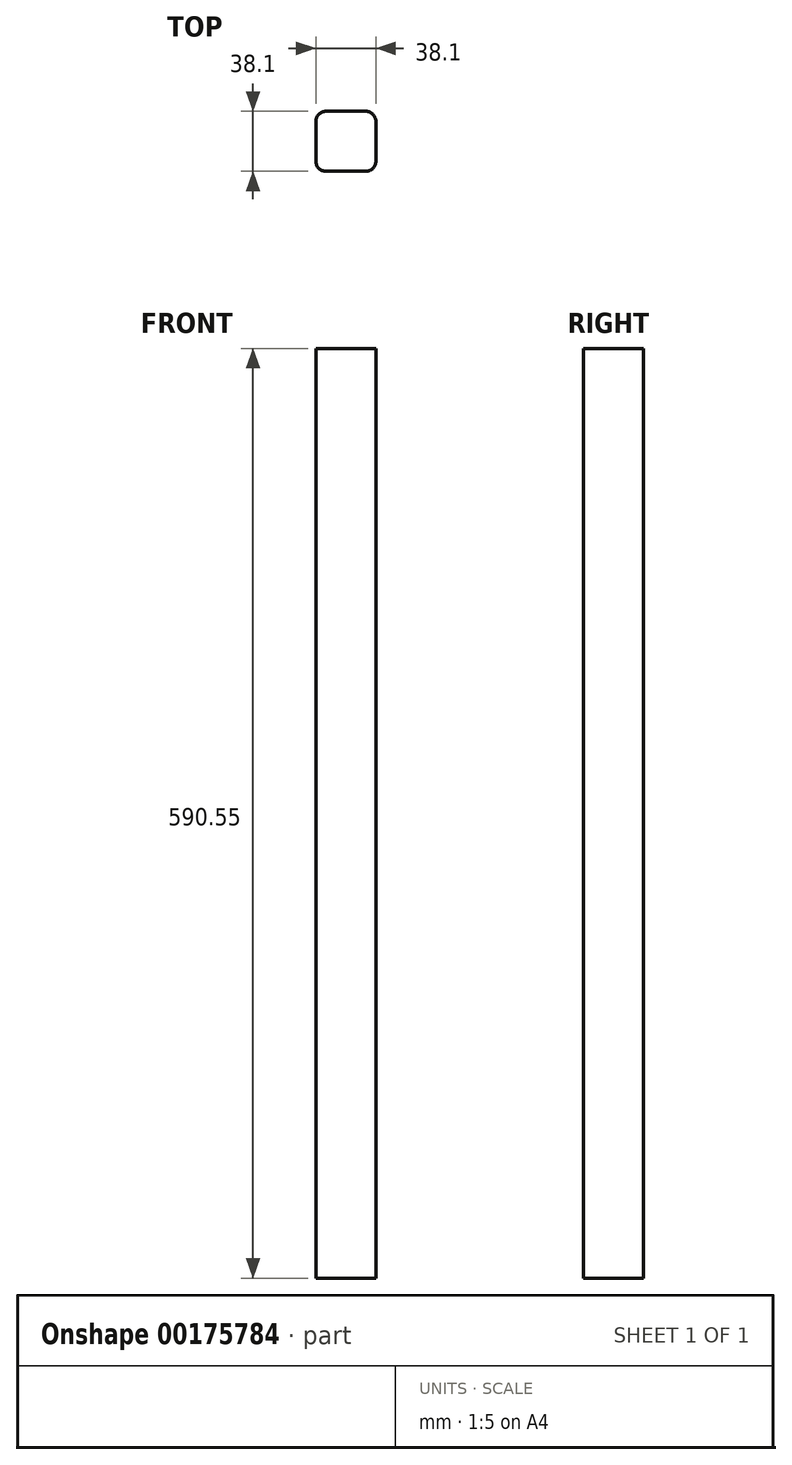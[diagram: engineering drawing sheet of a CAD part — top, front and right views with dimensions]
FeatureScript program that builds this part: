
annotation { "Feature Type Name" : "Feature", "Feature Type Description" : "" }
export const myFeature = defineFeature(function(context is Context, id is Id, definition is map)
    precondition{}
    {
        {
            var Q0;
            Q0=qCreatedBy(makeId("Top.planeOp"),FACE);
            var sketch = newSketch(context, id + "F0", { "sketchPlane" : qUnion([Q0])});
            skLineSegment(sketch, "E0.bottom", {"start": v(12.7, 19.05) * mm, "end": v(-12.7, 19.05) * mm});
            skLineSegment(sketch, "E0.top", {"start": v(12.7, -19.05) * mm, "end": v(-12.7, -19.05) * mm});
            skLineSegment(sketch, "E0.left", {"start": v(19.05, 12.7) * mm, "end": v(19.05, -12.7) * mm});
            skLineSegment(sketch, "E0.right", {"start": v(-19.05, 12.7) * mm, "end": v(-19.05, -12.7) * mm});
            skPoint(sketch, "E0.middle", {"position": v(0, 0) * mm});
            skPoint(sketch, "E1.visualSharp", {"position": v(-19.05, 19.05) * mm});
            skArc(sketch, "E1.filletArc", {"start": v(-12.7, 19.05) * mm, "mid": v(-17.2, 17.2) * mm, "end": v(-19.05, 12.7) * mm});
            skPoint(sketch, "E2.visualSharp", {"position": v(19.05, 19.05) * mm});
            skArc(sketch, "E2.filletArc", {"start": v(19.05, 12.7) * mm, "mid": v(17.2, 17.2) * mm, "end": v(12.7, 19.05) * mm});
            skPoint(sketch, "E3.visualSharp", {"position": v(19.05, -19.05) * mm});
            skArc(sketch, "E3.filletArc", {"start": v(12.7, -19.05) * mm, "mid": v(17.2, -17.2) * mm, "end": v(19.05, -12.7) * mm});
            skPoint(sketch, "E4.visualSharp", {"position": v(-19.05, -19.05) * mm});
            skArc(sketch, "E4.filletArc", {"start": v(-19.05, -12.7) * mm, "mid": v(-17.2, -17.2) * mm, "end": v(-12.7, -19.05) * mm});
            skSolve(sketch);
        }
        {
            var Q0;
            Q0 = qSketchRegion(id + "F0", true);
            extrude(context, id + "F1", {"entities" : qUnion([Q0]), "depth" : 590.55 * mm});
        }
    });
